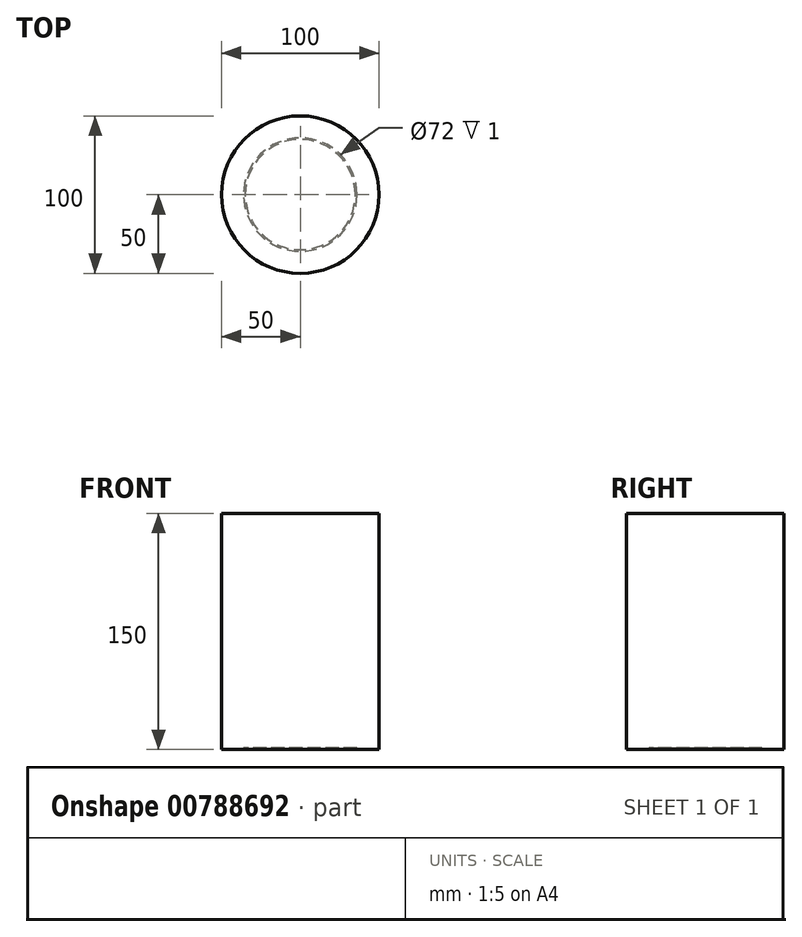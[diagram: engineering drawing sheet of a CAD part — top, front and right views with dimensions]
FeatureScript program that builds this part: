
annotation { "Feature Type Name" : "Feature", "Feature Type Description" : "" }
export const myFeature = defineFeature(function(context is Context, id is Id, definition is map)
    precondition{}
    {
        {
            assignVariable(context, id + "F0", {"name" : "Hight", "anyValue" : 150});
        }
        {
            assignVariable(context, id + "F1", {"name" : "Holehight", "anyValue" : 1});
        }
        {
            var Q0;
            Q0=qCreatedBy(makeId("Top.planeOp"),FACE);
            var sketch = newSketch(context, id + "F2", { "sketchPlane" : qUnion([Q0])});
            skCircle(sketch, "E0", {"center": v(0, 0) * mm, "radius": 50 * mm});
            skSolve(sketch);
        }
        {
            var Q0;
            Q0=makeQuery(id+"F2.imprint","IMPRINT",FACE,{"disambiguationData":[TD([[makeQuery(id+"F2.imprint","IMPRINT",EDGE,{"derivedFrom":sQuery(id+"F2.wireOp",EDGE,"E0")}),1.0]])]});
            extrude(context, id + "F3", {"entities" : qUnion([Q0]), "depth" : (getVariable(context, 'Hight')) * mm, "offsetDistance" : 25 * mm});
        }
        {
            var Q0;
            Q0=qCreatedBy(makeId("Top.planeOp"),FACE);
            var sketch = newSketch(context, id + "F4", { "sketchPlane" : qUnion([Q0])});
            skCircle(sketch, "E1", {"center": v(0, 0) * mm, "radius": 35 * mm});
            skCircle(sketch, "E2", {"center": v(0, 0) * mm, "radius": 36 * mm});
            skSolve(sketch);
        }
        {
            var Q0;
            Q0=makeQuery(id+"F4.imprint","IMPRINT",FACE,{"disambiguationData":[TD([[makeQuery(id+"F4.imprint","IMPRINT",EDGE,{"derivedFrom":sQuery(id+"F4.wireOp",EDGE,"E1")}),-1.0]])]});
            extrude(context, id + "F5", {"entities" : qUnion([Q0]), "operationType" : NewBodyOperationType.REMOVE, "depth" : (getVariable(context, 'Holehight')) * mm, "offsetDistance" : 25 * mm});
        }
    });
